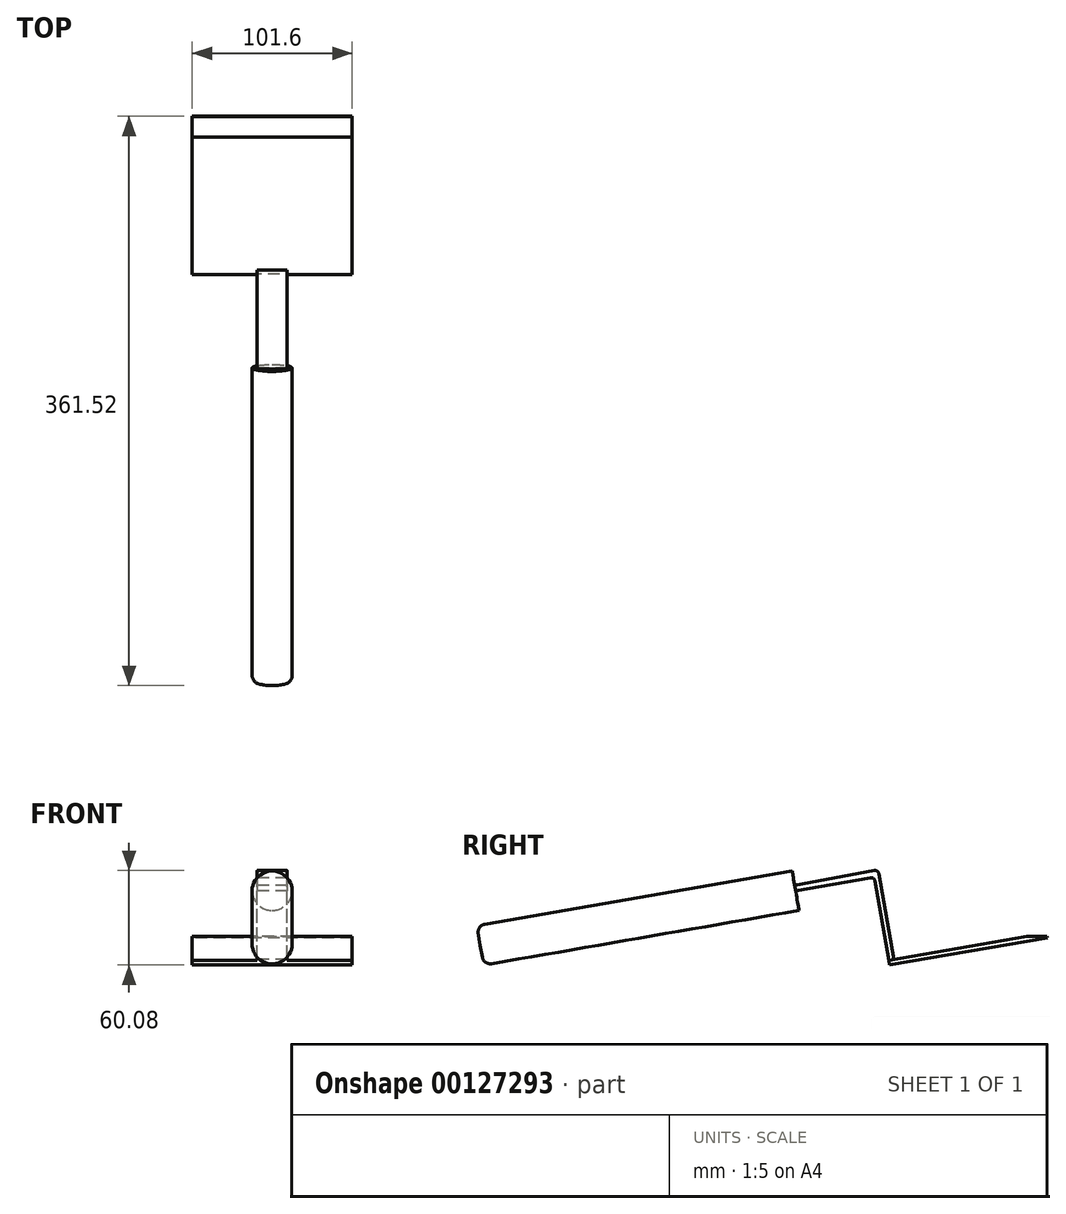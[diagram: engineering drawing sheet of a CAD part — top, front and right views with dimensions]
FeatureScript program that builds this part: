
annotation { "Feature Type Name" : "Feature", "Feature Type Description" : "" }
export const myFeature = defineFeature(function(context is Context, id is Id, definition is map)
    precondition{}
    {
        {
            var Q0;
            Q0=qCreatedBy(makeId("Right.planeOp"),FACE);
            var sketch = newSketch(context, id + "F0", { "sketchPlane" : qUnion([Q0])});
            skLineSegment(sketch, "E0", {"start": v(0, 0) * mm, "end": v(200.22, 34.66) * mm});
            skLineSegment(sketch, "E1", {"start": v(200.22, 34.66) * mm, "end": v(198.06, 47.18) * mm});
            skLineSegment(sketch, "E2", {"start": v(198.06, 47.18) * mm, "end": v(-2.4, 12.47) * mm});
            skLineSegment(sketch, "E3", {"start": v(-2.4, 12.47) * mm, "end": v(0, 0) * mm});
            skLineSegment(sketch, "E4", {"start": v(-2.4, 12.47) * mm, "end": v(227.5, 52.27) * mm, "construction": true});
            skSolve(sketch);
        }
        {
            var Q0;
            Q0 = qSketchRegion(id + "F0", true);
            var Q1;
            Q1=sQuery(id+"F0.wireOp",EDGE,"E4");
            revolve(context, id + "F1", {"entities" : qUnion([Q0]), "axis" : qUnion([Q1]), "revolveType" : RevolveType.FULL});
        }
        {
            var Q0;
            Q0=qCreatedBy(makeId("Right.planeOp"),FACE);
            var sketch = newSketch(context, id + "F2", { "sketchPlane" : qUnion([Q0])});
            skLineSegment(sketch, "E5", {"start": v(257.78, 0) * mm, "end": v(357.89, 17.33) * mm});
            skLineSegment(sketch, "E6", {"start": v(357.89, 17.33) * mm, "end": v(357.35, 20.46) * mm});
            skLineSegment(sketch, "E7", {"start": v(357.35, 20.46) * mm, "end": v(260.18, 3.64) * mm});
            skLineSegment(sketch, "E8", {"start": v(257.78, 0) * mm, "end": v(257.24, 3.13) * mm});
            skLineSegment(sketch, "E9", {"start": v(257.24, 3.13) * mm, "end": v(260.18, 3.64) * mm});
            skSolve(sketch);
        }
        {
            var Q0;
            Q0 = qSketchRegion(id + "F2", true);
            extrude(context, id + "F3", {"entities" : qUnion([Q0]), "endBound" : BoundingType.SYMMETRIC, "depth" : 101.6 * mm});
        }
        {
            var Q0;
            Q0=qCreatedBy(makeId("Right.planeOp"),FACE);
            var sketch = newSketch(context, id + "F4", { "sketchPlane" : qUnion([Q0])});
            skLineSegment(sketch, "E10", {"start": v(257.78, 0) * mm, "end": v(248.5, 53.37) * mm});
            skLineSegment(sketch, "E11", {"start": v(245.56, 55.44) * mm, "end": v(198.06, 47.18) * mm});
            skLineSegment(sketch, "E12", {"start": v(257.78, 0) * mm, "end": v(260.9, 0.54) * mm});
            skLineSegment(sketch, "E13", {"start": v(260.9, 0.54) * mm, "end": v(250.92, 57.98) * mm});
            skLineSegment(sketch, "E14", {"start": v(247.96, 60.04) * mm, "end": v(197.44, 50.73) * mm});
            skLineSegment(sketch, "E15", {"start": v(197.44, 50.73) * mm, "end": v(198.06, 47.18) * mm});
            skPoint(sketch, "E16.visualSharp", {"position": v(248.07, 55.87) * mm});
            skArc(sketch, "E16.filletArc", {"start": v(248.5, 53.37) * mm, "mid": v(247.46, 55) * mm, "end": v(245.56, 55.44) * mm});
            skPoint(sketch, "E17.visualSharp", {"position": v(250.48, 60.5) * mm});
            skArc(sketch, "E17.filletArc", {"start": v(250.92, 57.98) * mm, "mid": v(249.87, 59.63) * mm, "end": v(247.96, 60.04) * mm});
            skSolve(sketch);
        }
        {
            var Q0;
            Q0 = qSketchRegion(id + "F4", true);
            extrude(context, id + "F5", {"entities" : qUnion([Q0]), "operationType" : NewBodyOperationType.ADD, "endBound" : BoundingType.SYMMETRIC, "depth" : 19.05 * mm});
        }
        {
            var Q0;
            Q0=makeQuery(id+"F1.opRevolve","SWEPT_EDGE",EDGE,{"disambiguationData":[OSD([sQuery(id+"F0.wireOp",EDGE,"E0"),sQuery(id+"F0.wireOp",EDGE,"E3")])]});
            fillet(context, id + "F6", {"entities" : qUnion([Q0]), "radius" : 5.08 * mm, "tangentPropagation" : true, "allowEdgeOverflow" : false});
        }
        {
            var Q0;
            Q0=makeQuery(id+"F3.opExtrude","SWEPT_EDGE",EDGE,{"disambiguationData":[OSD([sQuery(id+"F2.wireOp",EDGE,"E6"),sQuery(id+"F2.wireOp",EDGE,"E7")])]});
            chamfer(context, id + "F7", {"entities" : qUnion([Q0]), "chamferType" : ChamferType.OFFSET_ANGLE, "width" : 12.7 * mm, "oppositeDirection" : false, "angle" : 10 * degree, "tangentPropagation" : true});
        }
        {
            var Q0;
            Q0=makeQuery(id+"F1.opRevolve","SWEPT_FACE",FACE,{"disambiguationData":[OSD([sQuery(id+"F0.wireOp",EDGE,"E1")])]});
            var sketch = newSketch(context, id + "F8", { "sketchPlane" : qUnion([Q0])});
            skLineSegment(sketch, "E18.0", {"start": v(-9.53, 16.31) * mm, "end": v(-9.53, 12.7) * mm});
            skLineSegment(sketch, "E18.1", {"start": v(-9.53, 12.7) * mm, "end": v(9.52, 12.7) * mm});
            skLineSegment(sketch, "E18.2", {"start": v(-9.53, 16.31) * mm, "end": v(9.52, 16.31) * mm});
            skLineSegment(sketch, "E18.3", {"start": v(9.53, 16.31) * mm, "end": v(9.53, 12.7) * mm});
            skSolve(sketch);
        }
        {
            var Q0;
            Q0 = qSketchRegion(id + "F8", true);
            extrude(context, id + "F9", {"entities" : qUnion([Q0]), "operationType" : NewBodyOperationType.REMOVE, "oppositeDirection" : true, "depth" : 50.8 * mm});
        }
        {
            var Q0;
            Q0=makeQuery(id+"F1.opRevolve","SWEPT_FACE",FACE,{"disambiguationData":[OSD([sQuery(id+"F0.wireOp",EDGE,"E1")])]});
            var sketch = newSketch(context, id + "F10", { "sketchPlane" : qUnion([Q0])});
            skLineSegment(sketch, "E19.0", {"start": v(-9.53, 16.31) * mm, "end": v(-9.53, 12.7) * mm});
            skLineSegment(sketch, "E19.1", {"start": v(-9.53, 12.7) * mm, "end": v(9.52, 12.7) * mm});
            skLineSegment(sketch, "E19.2", {"start": v(-9.53, 16.31) * mm, "end": v(9.52, 16.31) * mm});
            skLineSegment(sketch, "E19.3", {"start": v(9.53, 16.31) * mm, "end": v(9.53, 12.7) * mm});
            skSolve(sketch);
        }
        {
            var Q0;
            Q0 = qSketchRegion(id + "F10", true);
            extrude(context, id + "F11", {"entities" : qUnion([Q0]), "operationType" : NewBodyOperationType.ADD, "oppositeDirection" : true, "depth" : 50.8 * mm});
        }
    });
